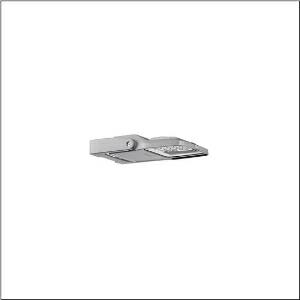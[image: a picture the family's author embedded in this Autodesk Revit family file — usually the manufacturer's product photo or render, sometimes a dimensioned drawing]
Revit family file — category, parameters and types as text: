
# Revit family: floodlight_fl_21_iq_micro___pl33t_5xa7761a4f2a_c8ff
name_source: partatom
category: Lighting Fixtures
units: mm (PartAtom-declared; Revit-internal decimal feet)

## family parameters
Cut with Voids When Loaded = No
Host = Face
Light Source = No
Part Type = Normal
Room Calculation Point = No
Round Connector Dimension = Use Diameter
Shared = No

## types (1)
- --- (1 x LED, 3050 lm, 23.1 W, 4000K)
    Apparent Load = 23 VA
    CIE Flux Codes = 26 75 99 100 100
    Color Rendering = 70
    Color Temperature = 4000K
    Default Elevation = 1800 mm
    Description = Floodlight FL 21 iQ micro, floodlight, primary light control with lens, of PMMA, primary optical cover: protective disc, of toughened safety glass, transparent, light distribution: PL33T, light emission: direct distribution, installation type: surface-mounted, LED, High Power LED, rated luminous flux: 3.050lm, luminous efficacy: 132lm/W, light colour: 740, colour temperature: 4000K, control gear: iQ Comfort/DALI, control: optimised constant luminous flux control (CLO 2.0), Desk-Remote (wireless, voltage-free reading and setting of iQ features in the workshop via application-optimized NFC function/RFID function), Light-Fading, Smart-Wire, Night-Set, Lumen-Switch, Temp-Guard, Auto-Match, with terminal, 6-pole, mains connection: 220..240V, AC, 50/60Hz, start of lifetime: 23W, end of service life: 24W, reduction: 11W, luminaire housing, of diecast aluminium, powder-coated, Siteco® metallic grey (DB 702S), corrosivity category C5 mid according to DIN EN ISO 12944, suitable for swimming pools, chlorine-resistant, sealing non-destructively replaceable, design bracket, of diecast aluminium, powder-coated, Siteco® metallic grey (DB 702S), protection rating (complete): IP66, insulation class (complete): insulation class II (safety insulation), certification: CE, ENEC, VDE, protection symbol: D, impact resistance: IK07, permissible operating ambient temperature: -40..+40°C, permissible operating ambient temperature for outdoor applications: -40..+50°C, standard: DIN EN 12944, LABS conformity tested according to VDMA 24364:2018-05, packaging unit: 1 piece

Light Distribution: PL33T
    Height = 65 mm
    Lamp = 1 x LED
    Lamp Light Flux = 3050 lm
    Lamp Power = 23.1 W
    Lamp count = 1
    Length = 312 mm
    Luminous efficacy = 132 lm/W
    Manufacturer = Siteco
    ModVariant = No
    Model = 5XA7761A4F2A
    Mounting Place = Wall
    Mounting Type = Surface mounted
    Number of Poles = 1
    OnlyDefault = Yes
    Power Factor = 1
    Product Name = Floodlight FL 21 iQ micro | PL33T
    Product group = floodlight | wall mounted
    ProductGroupID = 2001
    Protection Class = Protection class II
    Protection Degree = IP 66
    RLX_Detail_Level = 1
    RLX_Emergency_Light_Flux = 0 lm
    RLX_Emergency_Type = 0
    RLX_Emergency_Type_DB = No
    RlxData = <blob elided: 97429 chars, md5=13da4126>
    Socket = socket
    Standby Power = 0 W
    System Light Flux = 3050 lm
    System Power = 23 W
    Type Comments = factory setting: luminous flux: 100 % | dim-lin: 254 | 455 mA
    Type Image = l_1006878.jpg
    URL = http://relux.com
    VarID = @adj_148154
    Voltage = 0 V
    Weight = 0.00 kg
    Width = 230 mm

## geometry (parser evidence)
native form markers: Blend x4, Sweep x11
no freeform markers — native parametric forms only
